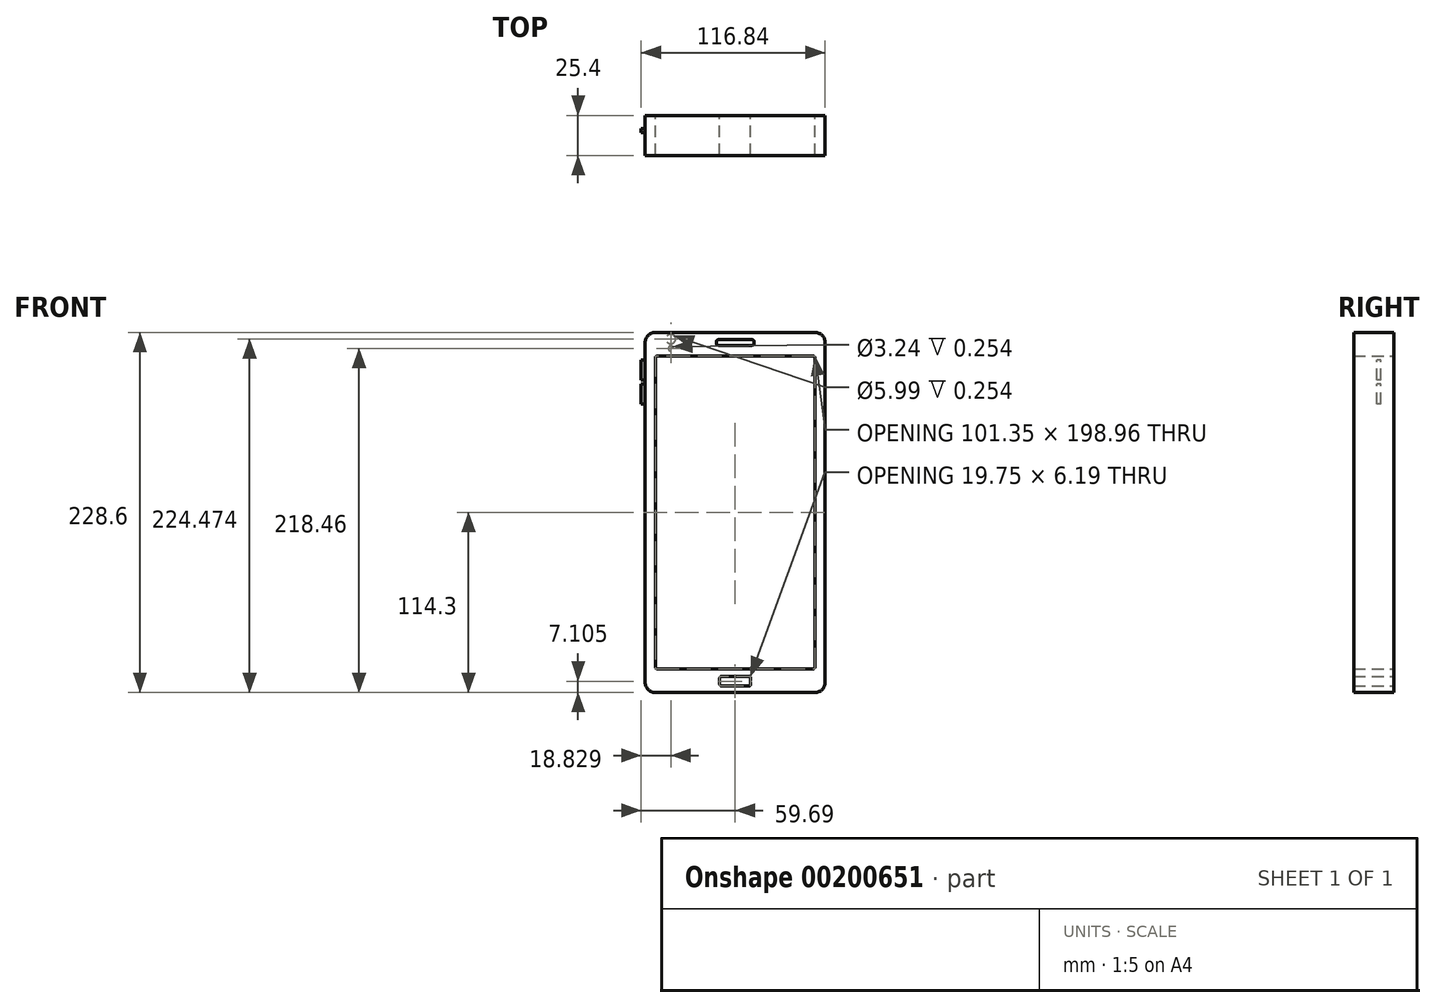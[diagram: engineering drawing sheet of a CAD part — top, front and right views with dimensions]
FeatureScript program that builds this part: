
annotation { "Feature Type Name" : "Feature", "Feature Type Description" : "" }
export const myFeature = defineFeature(function(context is Context, id is Id, definition is map)
    precondition{}
    {
        {
            var Q0;
            Q0=qCreatedBy(makeId("Front.planeOp"),FACE);
            var sketch = newSketch(context, id + "F0", { "sketchPlane" : qUnion([Q0])});
            skLineSegment(sketch, "E0.bottom", {"start": v(-50.8, 114.3) * mm, "end": v(50.8, 114.3) * mm});
            skLineSegment(sketch, "E0.top", {"start": v(-50.8, -114.3) * mm, "end": v(50.8, -114.3) * mm});
            skLineSegment(sketch, "E0.left", {"start": v(-57.15, 107.95) * mm, "end": v(-57.15, -107.95) * mm});
            skLineSegment(sketch, "E0.right", {"start": v(57.15, 107.95) * mm, "end": v(57.15, -107.95) * mm});
            skPoint(sketch, "E1.visualSharp", {"position": v(-57.15, 114.3) * mm});
            skArc(sketch, "E1.filletArc", {"start": v(-50.8, 114.3) * mm, "mid": v(-55.3, 112.44) * mm, "end": v(-57.15, 107.95) * mm});
            skPoint(sketch, "E2.visualSharp", {"position": v(57.15, 114.3) * mm});
            skArc(sketch, "E2.filletArc", {"start": v(57.15, 107.95) * mm, "mid": v(55.3, 112.44) * mm, "end": v(50.8, 114.3) * mm});
            skPoint(sketch, "E3.visualSharp", {"position": v(57.15, -114.3) * mm});
            skArc(sketch, "E3.filletArc", {"start": v(50.8, -114.3) * mm, "mid": v(55.3, -112.44) * mm, "end": v(57.15, -107.95) * mm});
            skPoint(sketch, "E4.visualSharp", {"position": v(-57.15, -114.3) * mm});
            skArc(sketch, "E4.filletArc", {"start": v(-57.15, -107.95) * mm, "mid": v(-55.3, -112.44) * mm, "end": v(-50.8, -114.3) * mm});
            skLineSegment(sketch, "E5.bottom", {"start": v(-49.37, 99.48) * mm, "end": v(49.37, 99.48) * mm});
            skLineSegment(sketch, "E5.top", {"start": v(-49.37, -99.48) * mm, "end": v(49.37, -99.48) * mm});
            skLineSegment(sketch, "E5.left", {"start": v(-50.67, 98.18) * mm, "end": v(-50.67, -98.18) * mm});
            skLineSegment(sketch, "E5.right", {"start": v(50.67, 98.18) * mm, "end": v(50.67, -98.18) * mm});
            skLineSegment(sketch, "E6.bottom", {"start": v(-8.57, -104.1) * mm, "end": v(8.57, -104.1) * mm});
            skLineSegment(sketch, "E6.top", {"start": v(-8.57, -110.29) * mm, "end": v(8.57, -110.29) * mm});
            skLineSegment(sketch, "E6.left", {"start": v(-9.87, -105.4) * mm, "end": v(-9.87, -108.99) * mm});
            skLineSegment(sketch, "E6.right", {"start": v(9.87, -105.4) * mm, "end": v(9.87, -108.99) * mm});
            skPoint(sketch, "E7.orphan", {"position": v(0, -74.4) * mm});
            skPoint(sketch, "E8.trimOffspring.end.orphan", {"position": v(0, -114.3) * mm});
            skPoint(sketch, "E9.visualSharp", {"position": v(-9.87, -104.1) * mm});
            skArc(sketch, "E9.filletArc", {"start": v(-8.57, -104.1) * mm, "mid": v(-9.5, -104.48) * mm, "end": v(-9.87, -105.4) * mm});
            skPoint(sketch, "E10.visualSharp", {"position": v(9.87, -104.1) * mm});
            skArc(sketch, "E10.filletArc", {"start": v(9.87, -105.4) * mm, "mid": v(9.5, -104.48) * mm, "end": v(8.57, -104.1) * mm});
            skPoint(sketch, "E11.visualSharp", {"position": v(9.87, -110.29) * mm});
            skArc(sketch, "E11.filletArc", {"start": v(8.57, -110.29) * mm, "mid": v(9.5, -109.9) * mm, "end": v(9.87, -108.99) * mm});
            skPoint(sketch, "E12.visualSharp", {"position": v(-9.87, -110.29) * mm});
            skArc(sketch, "E12.filletArc", {"start": v(-9.87, -108.99) * mm, "mid": v(-9.5, -109.9) * mm, "end": v(-8.57, -110.29) * mm});
            skPoint(sketch, "E13.visualSharp", {"position": v(-50.67, 99.48) * mm});
            skArc(sketch, "E13.filletArc", {"start": v(-49.37, 99.48) * mm, "mid": v(-50.3, 99.1) * mm, "end": v(-50.67, 98.18) * mm});
            skPoint(sketch, "E14.visualSharp", {"position": v(50.67, 99.48) * mm});
            skArc(sketch, "E14.filletArc", {"start": v(50.67, 98.18) * mm, "mid": v(50.3, 99.1) * mm, "end": v(49.37, 99.48) * mm});
            skPoint(sketch, "E15.visualSharp", {"position": v(50.67, -99.48) * mm});
            skArc(sketch, "E15.filletArc", {"start": v(49.37, -99.48) * mm, "mid": v(50.3, -99.1) * mm, "end": v(50.67, -98.18) * mm});
            skPoint(sketch, "E16.visualSharp", {"position": v(-50.67, -99.48) * mm});
            skArc(sketch, "E16.filletArc", {"start": v(-50.67, -98.18) * mm, "mid": v(-50.3, -99.1) * mm, "end": v(-49.37, -99.48) * mm});
            skPoint(sketch, "E17.centerSnap0", {"position": v(0, 114.3) * mm});
            skSolve(sketch);
        }
        {
            var Q0;
            Q0 = qSketchRegion(id + "F0", true);
            extrude(context, id + "F1", {"entities" : qUnion([Q0]), "depth" : 19.05 * mm});
        }
        {
            var Q0;
            Q0=makeQuery(id+"F1.opExtrude","SWEPT_FACE",FACE,{"disambiguationData":[OSD([sQuery(id+"F0.wireOp",EDGE,"E0.left")])]});
            var sketch = newSketch(context, id + "F2", { "sketchPlane" : qUnion([Q0])});
            skLineSegment(sketch, "E18.bottom", {"start": v(8.26, 83.98) * mm, "end": v(10.8, 83.98) * mm});
            skLineSegment(sketch, "E18.top", {"start": v(8.26, 96.68) * mm, "end": v(10.8, 96.68) * mm});
            skLineSegment(sketch, "E18.left", {"start": v(8.26, 83.98) * mm, "end": v(8.26, 96.68) * mm});
            skLineSegment(sketch, "E18.right", {"start": v(10.8, 83.98) * mm, "end": v(10.8, 96.68) * mm});
            skPoint(sketch, "E18.middle", {"position": v(9.53, 90.33) * mm});
            skPoint(sketch, "E18.middle.positionSnap0", {"position": v(9.53, 107.95) * mm});
            skPoint(sketch, "E18.centerSnap0", {"position": v(9.53, 107.95) * mm});
            skLineSegment(sketch, "E19.bottom", {"start": v(8.25, 68.74) * mm, "end": v(10.8, 68.74) * mm});
            skLineSegment(sketch, "E19.top", {"start": v(8.25, 81.44) * mm, "end": v(10.8, 81.44) * mm});
            skLineSegment(sketch, "E19.left", {"start": v(8.26, 68.74) * mm, "end": v(8.25, 81.44) * mm});
            skLineSegment(sketch, "E19.right", {"start": v(10.8, 68.74) * mm, "end": v(10.8, 81.44) * mm});
            skPoint(sketch, "E19.middle", {"position": v(9.53, 75.09) * mm});
            skPoint(sketch, "E19.middle.positionSnap0", {"position": v(9.53, -107.95) * mm});
            skPoint(sketch, "E19.centerSnap0", {"position": v(9.53, -107.95) * mm});
            skSolve(sketch);
        }
        {
            var Q0;
            Q0=makeQuery(id+"F2.imprint","IMPRINT",FACE,{"disambiguationData":[TD([[makeQuery(id+"F2.imprint","IMPRINT",EDGE,{"derivedFrom":sQuery(id+"F2.wireOp",EDGE,"E18.bottom")}),1.0]])]});
            var Q1;
            Q1=makeQuery(id+"F2.imprint","IMPRINT",FACE,{"disambiguationData":[TD([[makeQuery(id+"F2.imprint","IMPRINT",EDGE,{"derivedFrom":sQuery(id+"F2.wireOp",EDGE,"E19.bottom")}),1.0]])]});
            extrude(context, id + "F3", {"entities" : qUnion([Q0, Q1]), "operationType" : NewBodyOperationType.ADD, "depth" : 2.54 * mm});
        }
        {
            var Q0;
            Q0 = qSketchRegion(id + "F0", true);
            extrude(context, id + "F4", {"entities" : qUnion([Q0]), "operationType" : NewBodyOperationType.ADD, "depth" : 25.4 * mm});
        }
        {
            var Q0;
            Q0 = qSketchRegion(id + "F0", true);
            extrude(context, id + "F5", {"entities" : qUnion([Q0]), "operationType" : NewBodyOperationType.ADD, "depth" : 25.4 * mm});
        }
        {
            var Q0;
            Q0=makeQuery(id+"F4.opExtrude","CAP_FACE",FACE,{"disambiguationData":[OSD([sQuery(id+"F0.wireOp",EDGE,"E0.bottom"),sQuery(id+"F0.wireOp",EDGE,"E0.top"),sQuery(id+"F0.wireOp",EDGE,"E0.left"),sQuery(id+"F0.wireOp",EDGE,"E0.right"),sQuery(id+"F0.wireOp",EDGE,"E1.filletArc"),sQuery(id+"F0.wireOp",EDGE,"E2.filletArc"),sQuery(id+"F0.wireOp",EDGE,"E3.filletArc"),sQuery(id+"F0.wireOp",EDGE,"E4.filletArc"),sQuery(id+"F0.wireOp",EDGE,"E5.bottom"),sQuery(id+"F0.wireOp",EDGE,"E5.top"),sQuery(id+"F0.wireOp",EDGE,"E5.left"),sQuery(id+"F0.wireOp",EDGE,"E5.right"),sQuery(id+"F0.wireOp",EDGE,"E6.bottom"),sQuery(id+"F0.wireOp",EDGE,"E6.top"),sQuery(id+"F0.wireOp",EDGE,"E6.left"),sQuery(id+"F0.wireOp",EDGE,"E6.right"),sQuery(id+"F0.wireOp",EDGE,"E9.filletArc"),sQuery(id+"F0.wireOp",EDGE,"E10.filletArc"),sQuery(id+"F0.wireOp",EDGE,"E11.filletArc"),sQuery(id+"F0.wireOp",EDGE,"E12.filletArc"),sQuery(id+"F0.wireOp",EDGE,"E13.filletArc"),sQuery(id+"F0.wireOp",EDGE,"E14.filletArc"),sQuery(id+"F0.wireOp",EDGE,"E15.filletArc"),sQuery(id+"F0.wireOp",EDGE,"E16.filletArc")])],"isStart":false});
            var sketch = newSketch(context, id + "F6", { "sketchPlane" : qUnion([Q0])});
            skLineSegment(sketch, "E20.bottom", {"start": v(-10.73, 106.19) * mm, "end": v(10.73, 106.19) * mm});
            skLineSegment(sketch, "E20.top", {"start": v(-10.73, 109.71) * mm, "end": v(10.73, 109.71) * mm});
            skLineSegment(sketch, "E20.left", {"start": v(-12.03, 107.48) * mm, "end": v(-12.03, 108.42) * mm});
            skLineSegment(sketch, "E20.right", {"start": v(12.03, 107.48) * mm, "end": v(12.03, 108.42) * mm});
            skPoint(sketch, "E20.middle", {"position": v(0, 107.95) * mm});
            skPoint(sketch, "E20.middle.positionSnap0", {"position": v(0, 114.3) * mm});
            skPoint(sketch, "E20.centerSnap0", {"position": v(0, 114.3) * mm});
            skPoint(sketch, "E21.visualSharp", {"position": v(-12.03, 109.71) * mm});
            skArc(sketch, "E21.filletArc", {"start": v(-10.73, 109.71) * mm, "mid": v(-11.65, 109.33) * mm, "end": v(-12.03, 108.42) * mm});
            skPoint(sketch, "E22.visualSharp", {"position": v(12.03, 109.71) * mm});
            skArc(sketch, "E22.filletArc", {"start": v(12.03, 108.42) * mm, "mid": v(11.65, 109.33) * mm, "end": v(10.73, 109.71) * mm});
            skPoint(sketch, "E23.visualSharp", {"position": v(12.03, 106.19) * mm});
            skArc(sketch, "E23.filletArc", {"start": v(10.73, 106.19) * mm, "mid": v(11.65, 106.57) * mm, "end": v(12.03, 107.48) * mm});
            skPoint(sketch, "E24.visualSharp", {"position": v(-12.03, 106.19) * mm});
            skArc(sketch, "E24.filletArc", {"start": v(-12.03, 107.48) * mm, "mid": v(-11.65, 106.57) * mm, "end": v(-10.73, 106.19) * mm});
            skSolve(sketch);
        }
        {
            var Q0;
            Q0=makeQuery(id+"F6.imprint","IMPRINT",FACE,{"disambiguationData":[TD([[makeQuery(id+"F6.imprint","IMPRINT",EDGE,{"derivedFrom":sQuery(id+"F6.wireOp",EDGE,"E20.bottom")}),1.0]])]});
            extrude(context, id + "F7", {"entities" : qUnion([Q0]), "operationType" : NewBodyOperationType.REMOVE, "oppositeDirection" : true, "depth" : 0.25 * mm});
        }
        {
            var Q0;
            Q0=makeQuery(id+"F0.imprint","IMPRINT",FACE,{"disambiguationData":[TD([[makeQuery(id+"F0.imprint","IMPRINT",EDGE,{"derivedFrom":sQuery(id+"F0.wireOp",EDGE,"E0.bottom")}),-1.0]])]});
            var sketch = newSketch(context, id + "F8", { "sketchPlane" : qUnion([Q0])});
            skCircle(sketch, "E25", {"center": v(-40.86, 110.17) * mm, "radius": 3 * mm});
            skCircle(sketch, "E26", {"center": v(-40.86, 104.16) * mm, "radius": 1.62 * mm});
            skSolve(sketch);
        }
        {
            var Q0;
            Q0 = qSketchRegion(id + "F8", true);
            extrude(context, id + "F9", {"entities" : qUnion([Q0]), "operationType" : NewBodyOperationType.REMOVE, "depth" : 0.25 * mm});
        }
    });
